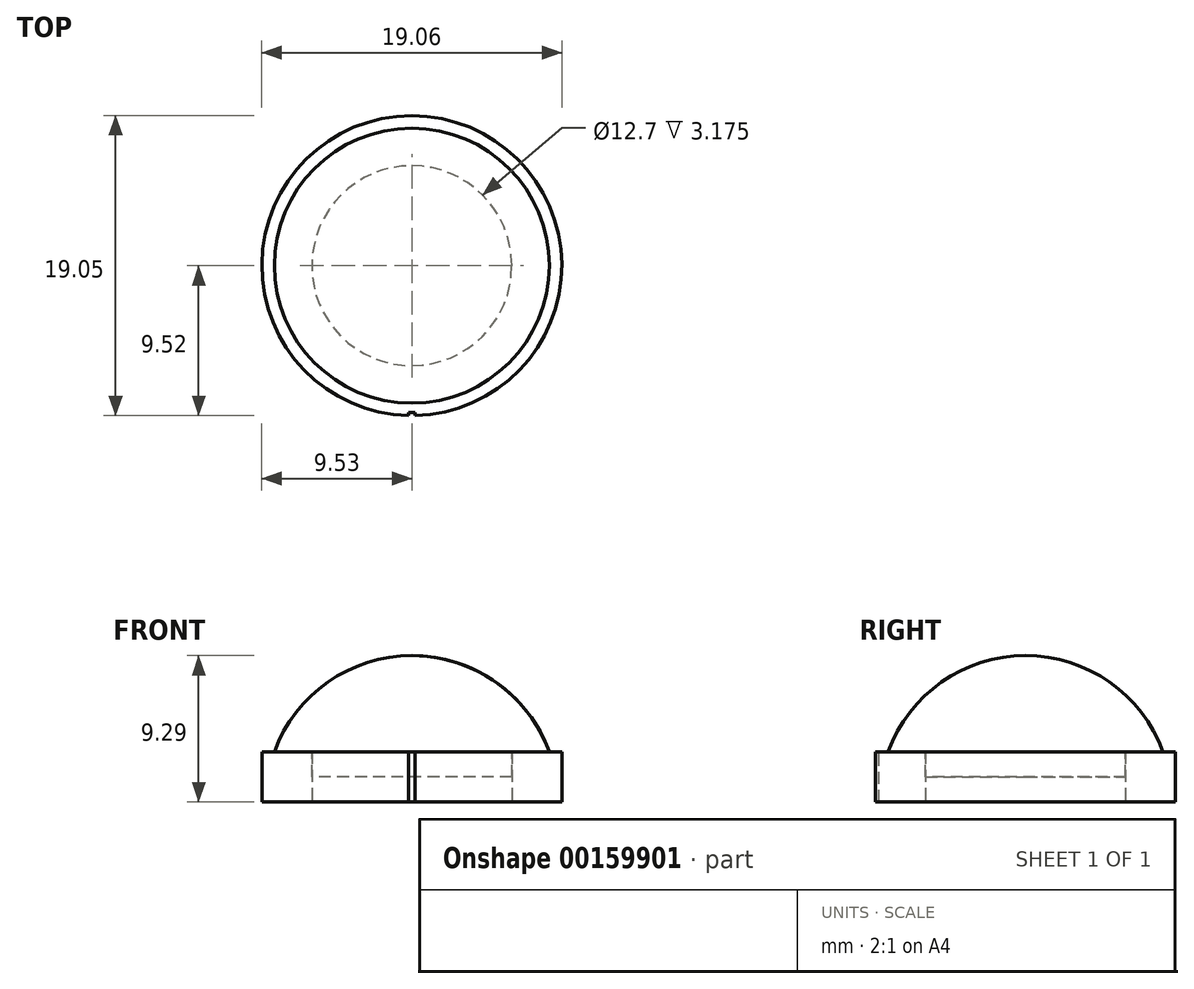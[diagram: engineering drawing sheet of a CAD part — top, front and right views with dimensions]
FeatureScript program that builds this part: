
annotation { "Feature Type Name" : "Feature", "Feature Type Description" : "" }
export const myFeature = defineFeature(function(context is Context, id is Id, definition is map)
    precondition{}
    {
        {
            var Q0;
            Q0=qCreatedBy(makeId("Top.planeOp"),FACE);
            var sketch = newSketch(context, id + "F0", { "sketchPlane" : qUnion([Q0])});
            skCircle(sketch, "E0", {"center": v(0, 0) * mm, "radius": 9.53 * mm});
            skCircle(sketch, "E1", {"center": v(0, 0) * mm, "radius": 6.35 * mm});
            skSolve(sketch);
        }
        {
            var Q0;
            Q0=makeQuery(id+"F0.imprint","IMPRINT",FACE,{"disambiguationData":[TD([[makeQuery(id+"F0.imprint","IMPRINT",EDGE,{"derivedFrom":sQuery(id+"F0.wireOp",EDGE,"E0")}),1.0]])]});
            extrude(context, id + "F1", {"entities" : qUnion([Q0]), "depth" : 3.17 * mm});
        }
        {
            var Q0;
            Q0=qCreatedBy(makeId("Front.planeOp"),FACE);
            var sketch = newSketch(context, id + "F2", { "sketchPlane" : qUnion([Q0])});
            skLineSegment(sketch, "E2", {"start": v(0, 0) * mm, "end": v(0, 1.59) * mm, "construction": true});
            skLineSegment(sketch, "E3", {"start": v(0, 1.59) * mm, "end": v(6.35, 1.59) * mm});
            skLineSegment(sketch, "E4", {"start": v(6.35, 1.59) * mm, "end": v(6.35, 3.18) * mm});
            skLineSegment(sketch, "E5", {"start": v(6.35, 3.18) * mm, "end": v(8.73, 3.18) * mm});
            skArc(sketch, "E6", {"start": v(8.73, 3.18) * mm, "mid": v(5.33, 7.6) * mm, "end": v(0, 9.3) * mm});
            skLineSegment(sketch, "E7", {"start": v(0, 9.3) * mm, "end": v(0, 1.59) * mm});
            skSolve(sketch);
        }
        {
            var Q0;
            Q0=makeQuery(id+"F2.imprint","IMPRINT",FACE,{"disambiguationData":[TD([[makeQuery(id+"F2.imprint","IMPRINT",EDGE,{"derivedFrom":sQuery(id+"F2.wireOp",EDGE,"E4")}),1.0]])]});
            var Q1;
            Q1=sQuery(id+"F2.wireOp",EDGE,"E7");
            revolve(context, id + "F3", {"entities" : qUnion([Q0]), "axis" : qUnion([Q1]), "revolveType" : RevolveType.FULL});
        }
        {
            var Q0;
            Q0=makeQuery(id+"F1.opExtrude","CAP_FACE",FACE,{"disambiguationData":[OSD([sQuery(id+"F0.wireOp",EDGE,"E0"),sQuery(id+"F0.wireOp",EDGE,"E1")])],"isStart":false});
            var sketch = newSketch(context, id + "F4", { "sketchPlane" : qUnion([Q0])});
            skLineSegment(sketch, "E8", {"start": v(0, 0) * mm, "end": v(0, -9.53) * mm, "construction": true});
            skLineSegment(sketch, "E9.bottom", {"start": v(0.2, -9.33) * mm, "end": v(-0.2, -9.33) * mm});
            skLineSegment(sketch, "E9.top", {"start": v(0.2, -9.72) * mm, "end": v(-0.2, -9.72) * mm});
            skLineSegment(sketch, "E9.left", {"start": v(0.2, -9.33) * mm, "end": v(0.2, -9.72) * mm});
            skLineSegment(sketch, "E9.right", {"start": v(-0.2, -9.33) * mm, "end": v(-0.2, -9.72) * mm});
            skPoint(sketch, "E9.middle", {"position": v(0, -9.53) * mm});
            skSolve(sketch);
        }
        {
            var Q0;
            {var subQ0=sQuery(id+"F4.wireOp",EDGE,"E9.bottom");Q0=makeQuery(id+"F4.imprint","IMPRINT",FACE,{"disambiguationData":[TD([[makeQuery(id+"F4.imprint","IMPRINT",EDGE,{"derivedFrom":subQ0}),1.0]])]});}
            var Q1;
            {var subQ0=sQuery(id+"F4.wireOp",EDGE,"E9.top");Q1=makeQuery(id+"F4.imprint","IMPRINT",FACE,{"disambiguationData":[TD([[makeQuery(id+"F4.imprint","IMPRINT",EDGE,{"derivedFrom":subQ0}),-1.0]])]});}
            extrude(context, id + "F5", {"entities" : qUnion([Q0, Q1]), "operationType" : NewBodyOperationType.REMOVE, "oppositeDirection" : true, "depth" : 25.4 * mm});
        }
    });
